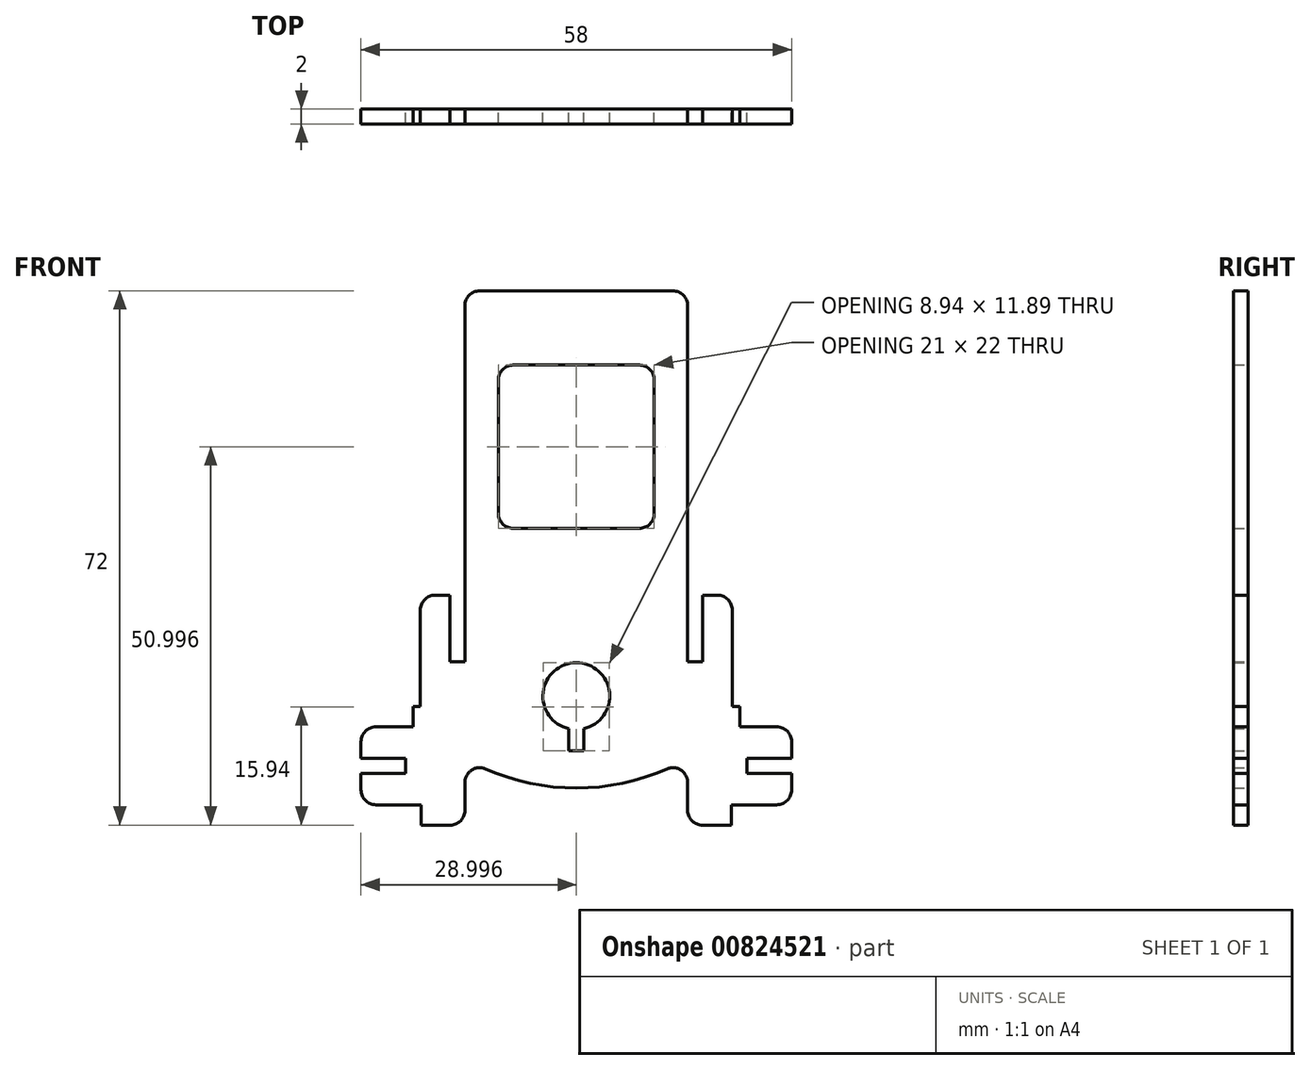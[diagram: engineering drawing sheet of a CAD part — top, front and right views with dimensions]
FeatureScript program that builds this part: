
annotation { "Feature Type Name" : "Feature", "Feature Type Description" : "" }
export const myFeature = defineFeature(function(context is Context, id is Id, definition is map)
    precondition{}
    {
        {
            var Q0;
            Q0=qCreatedBy(makeId("Front.planeOp"),FACE);
            var sketch = newSketch(context, id + "F0", { "sketchPlane" : qUnion([Q0])});
            skLineSegment(sketch, "E0.left", {"start": v(-13, 17.99) * mm, "end": v(-13, -0.01) * mm});
            skLineSegment(sketch, "E0.right", {"start": v(17, 17.99) * mm, "end": v(17, -0.01) * mm});
            skPoint(sketch, "E0.middle", {"position": v(2, 2.49) * mm});
            skPoint(sketch, "E1", {"position": v(2, -17.01) * mm});
            skPoint(sketch, "E1.positionSnap0", {"position": v(2, -13.01) * mm});
            skArc(sketch, "E2", {"start": v(-10.2, -14.44) * mm, "mid": v(2, -17.01) * mm, "end": v(14.19, -14.44) * mm});
            skLineSegment(sketch, "E3", {"start": v(1, -12.01) * mm, "end": v(3, -12.01) * mm});
            skLineSegment(sketch, "E4", {"start": v(1, -12.01) * mm, "end": v(1, -9.01) * mm});
            skLineSegment(sketch, "E5", {"start": v(3, -12.01) * mm, "end": v(3, -9.01) * mm});
            skArc(sketch, "E6", {"start": v(3, -9.01) * mm, "mid": v(2, -0.13) * mm, "end": v(1, -9.01) * mm});
            skLineSegment(sketch, "E7", {"start": v(-13, -0.01) * mm, "end": v(-15, -0.01) * mm});
            skLineSegment(sketch, "E8", {"start": v(-15, -0.01) * mm, "end": v(-15, 8.99) * mm});
            skLineSegment(sketch, "E9", {"start": v(-15, 8.99) * mm, "end": v(-17, 8.99) * mm});
            skLineSegment(sketch, "E10", {"start": v(-18.88, -22.01) * mm, "end": v(-15, -22.01) * mm});
            skLineSegment(sketch, "E11", {"start": v(-19, 6.99) * mm, "end": v(-19, -6.01) * mm});
            skLineSegment(sketch, "E12", {"start": v(-19, -6.01) * mm, "end": v(-20, -6.01) * mm});
            skLineSegment(sketch, "E13", {"start": v(-18.88, -22.01) * mm, "end": v(-18.88, -19.26) * mm});
            skLineSegment(sketch, "E14.bottom", {"start": v(-25, -8.76) * mm, "end": v(-20, -8.76) * mm});
            skLineSegment(sketch, "E14.top", {"start": v(-25, -19.26) * mm, "end": v(-18.88, -19.26) * mm});
            skLineSegment(sketch, "E14.left", {"start": v(-27, -10.76) * mm, "end": v(-27, -13.01) * mm});
            skPoint(sketch, "E14.middle", {"position": v(-18.88, -14.01) * mm});
            skLineSegment(sketch, "E15", {"start": v(-20, -6.01) * mm, "end": v(-20, -8.76) * mm});
            skLineSegment(sketch, "E16", {"start": v(-13, -20.01) * mm, "end": v(-13, -16.27) * mm});
            skPoint(sketch, "E16.startSnap0", {"position": v(-8.44, -22.01) * mm});
            skPoint(sketch, "E17.trimOffspring.end.orphan", {"position": v(-10.75, -19.26) * mm});
            skPoint(sketch, "E18.trimOffspring.end.orphan", {"position": v(-10.75, -8.76) * mm});
            skPoint(sketch, "E19.trimOffspring.end.orphan", {"position": v(-18.88, -6.01) * mm});
            skLineSegment(sketch, "E20", {"start": v(-27, -13.01) * mm, "end": v(-21, -13.01) * mm});
            skLineSegment(sketch, "E21", {"start": v(-27, -15.01) * mm, "end": v(-21, -15.01) * mm});
            skLineSegment(sketch, "E22", {"start": v(-21, -15.01) * mm, "end": v(-21, -13.01) * mm});
            skLineSegment(sketch, "E23.trimOffspring", {"start": v(-27, -15.01) * mm, "end": v(-27, -17.26) * mm});
            skPoint(sketch, "E24.newPointA", {"position": v(2, -22.01) * mm});
            skPoint(sketch, "E24.newPointB", {"position": v(-13, -22.01) * mm});
            skArc(sketch, "E24.filletArc", {"start": v(-15, -22.01) * mm, "mid": v(-13.59, -21.43) * mm, "end": v(-13, -20.01) * mm});
            skPoint(sketch, "E25.visualSharp", {"position": v(-13, -13.01) * mm});
            skArc(sketch, "E25.filletArc", {"start": v(-10.2, -14.44) * mm, "mid": v(-12.1, -14.6) * mm, "end": v(-13, -16.27) * mm});
            skPoint(sketch, "E26.visualSharp", {"position": v(-19, 8.99) * mm});
            skArc(sketch, "E26.filletArc", {"start": v(-17, 8.99) * mm, "mid": v(-18.42, 8.4) * mm, "end": v(-19, 6.99) * mm});
            skPoint(sketch, "E27.visualSharp", {"position": v(-27, -8.76) * mm});
            skArc(sketch, "E27.filletArc", {"start": v(-25, -8.76) * mm, "mid": v(-26.42, -9.35) * mm, "end": v(-27, -10.76) * mm});
            skPoint(sketch, "E28.visualSharp", {"position": v(-27, -19.26) * mm});
            skArc(sketch, "E28.filletArc", {"start": v(-27, -17.26) * mm, "mid": v(-26.42, -18.68) * mm, "end": v(-25, -19.26) * mm});
            skLineSegment(sketch, "E29.MirrorCS", {"start": v(17, -0.01) * mm, "end": v(19, -0.01) * mm});
            skLineSegment(sketch, "E30.MirrorCS", {"start": v(19, -0.01) * mm, "end": v(19, 8.99) * mm});
            skLineSegment(sketch, "E31.MirrorCS", {"start": v(19, 8.99) * mm, "end": v(21, 8.99) * mm});
            skArc(sketch, "E32.MirrorCS", {"start": v(21, 8.99) * mm, "mid": v(22.41, 8.4) * mm, "end": v(23, 6.99) * mm});
            skLineSegment(sketch, "E33.MirrorCS", {"start": v(23, 6.99) * mm, "end": v(23, -6.01) * mm});
            skLineSegment(sketch, "E34.MirrorCS", {"start": v(23, -6.01) * mm, "end": v(24, -6.01) * mm});
            skLineSegment(sketch, "E35.MirrorCS", {"start": v(24, -6.01) * mm, "end": v(24, -8.76) * mm});
            skLineSegment(sketch, "E36.MirrorCS", {"start": v(29, -8.76) * mm, "end": v(24, -8.76) * mm});
            skArc(sketch, "E37.MirrorCS", {"start": v(29, -8.76) * mm, "mid": v(30.41, -9.35) * mm, "end": v(31, -10.76) * mm});
            skLineSegment(sketch, "E38.MirrorCS", {"start": v(31, -10.76) * mm, "end": v(31, -13.01) * mm});
            skLineSegment(sketch, "E39.MirrorCS", {"start": v(31, -13.01) * mm, "end": v(25, -13.01) * mm});
            skLineSegment(sketch, "E40.MirrorCS", {"start": v(25, -15.01) * mm, "end": v(25, -13.01) * mm});
            skLineSegment(sketch, "E41.MirrorCS", {"start": v(31, -15.01) * mm, "end": v(25, -15.01) * mm});
            skLineSegment(sketch, "E42.MirrorCS", {"start": v(31, -15.01) * mm, "end": v(31, -17.26) * mm});
            skArc(sketch, "E43.MirrorCS", {"start": v(31, -17.26) * mm, "mid": v(30.41, -18.68) * mm, "end": v(29, -19.26) * mm});
            skLineSegment(sketch, "E44.MirrorCS", {"start": v(29, -19.26) * mm, "end": v(22.87, -19.26) * mm});
            skLineSegment(sketch, "E45.MirrorCS", {"start": v(22.87, -22.01) * mm, "end": v(22.87, -19.26) * mm});
            skLineSegment(sketch, "E46.MirrorCS", {"start": v(22.87, -22.01) * mm, "end": v(19, -22.01) * mm});
            skArc(sketch, "E47.MirrorCS", {"start": v(19, -22.01) * mm, "mid": v(17.58, -21.43) * mm, "end": v(17, -20.01) * mm});
            skLineSegment(sketch, "E48.MirrorCS", {"start": v(17, -20.01) * mm, "end": v(17, -16.27) * mm});
            skArc(sketch, "E49.MirrorCS", {"start": v(14.19, -14.44) * mm, "mid": v(16.09, -14.6) * mm, "end": v(17, -16.27) * mm});
            skPoint(sketch, "E50.orphan", {"position": v(17, -13.01) * mm});
            skPoint(sketch, "E51.start.orphan", {"position": v(2, 17.99) * mm});
            skLineSegment(sketch, "E52", {"start": v(-11, 49.99) * mm, "end": v(15, 49.99) * mm});
            skLineSegment(sketch, "E53", {"start": v(-13, 17.99) * mm, "end": v(-13, 47.99) * mm});
            skLineSegment(sketch, "E54", {"start": v(17, 17.99) * mm, "end": v(17, 47.99) * mm});
            skLineSegment(sketch, "E55", {"start": v(-6.5, 39.99) * mm, "end": v(10.5, 39.99) * mm});
            skLineSegment(sketch, "E56", {"start": v(12.5, 37.99) * mm, "end": v(12.5, 19.99) * mm});
            skLineSegment(sketch, "E57", {"start": v(10.5, 17.99) * mm, "end": v(-6.5, 17.99) * mm});
            skLineSegment(sketch, "E58", {"start": v(-8.5, 19.99) * mm, "end": v(-8.5, 37.99) * mm});
            skPoint(sketch, "E59.visualSharp", {"position": v(-13, 49.99) * mm});
            skArc(sketch, "E59.filletArc", {"start": v(-11, 49.99) * mm, "mid": v(-12.42, 49.4) * mm, "end": v(-13, 47.99) * mm});
            skPoint(sketch, "E60.visualSharp", {"position": v(17, 49.99) * mm});
            skArc(sketch, "E60.filletArc", {"start": v(17, 47.99) * mm, "mid": v(16.41, 49.4) * mm, "end": v(15, 49.99) * mm});
            skPoint(sketch, "E61.visualSharp", {"position": v(-8.5, 39.99) * mm});
            skArc(sketch, "E61.filletArc", {"start": v(-6.5, 39.99) * mm, "mid": v(-7.92, 39.4) * mm, "end": v(-8.5, 37.99) * mm});
            skPoint(sketch, "E62.visualSharp", {"position": v(12.5, 39.99) * mm});
            skArc(sketch, "E62.filletArc", {"start": v(12.5, 37.99) * mm, "mid": v(11.91, 39.4) * mm, "end": v(10.5, 39.99) * mm});
            skPoint(sketch, "E63.visualSharp", {"position": v(-8.5, 17.99) * mm});
            skArc(sketch, "E63.filletArc", {"start": v(-8.5, 19.99) * mm, "mid": v(-7.92, 18.57) * mm, "end": v(-6.5, 17.99) * mm});
            skPoint(sketch, "E64.visualSharp", {"position": v(12.5, 17.99) * mm});
            skArc(sketch, "E64.filletArc", {"start": v(10.5, 17.99) * mm, "mid": v(11.91, 18.57) * mm, "end": v(12.5, 19.99) * mm});
            skSolve(sketch);
        }
        {
            var Q0;
            Q0 = qSketchRegion(id + "F0", true);
            extrude(context, id + "F1", {"entities" : qUnion([Q0]), "depth" : 2 * mm, "offsetDistance" : 25 * mm});
        }
    });
